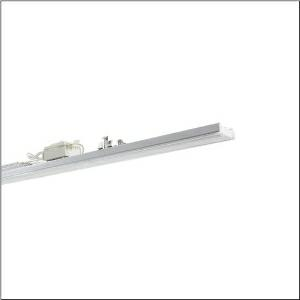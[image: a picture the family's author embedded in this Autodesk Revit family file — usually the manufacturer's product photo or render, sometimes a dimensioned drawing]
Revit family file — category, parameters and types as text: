
# Revit family: licross_11_recessed_ho_51tl11dn4exs
name_source: partatom
category: Lighting Fixtures
units: mm (PartAtom-declared; Revit-internal decimal feet)

## family parameters
Cut with Voids When Loaded = No
Host = Face
Light Source = No
Part Type = Normal
Room Calculation Point = No
Round Connector Dimension = Use Diameter
Shared = No

## types (1)
- --- (1 x LED, 14000 lm, 76.8 W, 4000K)
    Apparent Load = 77 VA
    CIE Flux Codes = 87 95 99 100 100
    Color Rendering = 80
    Color Temperature = 4000K
    Default Elevation = 1800 mm
    Description = Licross 11 Recessed HO, luminaire insert, of sheet steel, coil coated, white, length: 1.500mm, width: 66mm, height: 67mm, LED rated luminous flux: 14.000lm, light colour: 840, SDCM (Standard Deviation of Colour Matching)MacAdam ≤ 2 SDCM (initial), control gear: DALI 2, with plug, 5-pole, with phase selection, mains connection: 220..240V, AC, 50/60Hz, rated input power: 77W, internal wiring halogen-free, primary light control with lens, of plastic, primary optical cover: cover, of PMMA, light emission: direct distribution, primary light characteristic: symmetric, protection rating (complete): IP40, insulation class (complete): insulation class I (protective earthing), certification: CE, ENEC, VDE, UKCA, protection symbol: D if used in an environment without relevant dust loads with corresponding accessories, impact resistance: IK06, permissible ambient temperature for indoor applications: -25..+30°C, corresponds to IFS (International Featured Standards) requirements for safety and quality in the food industry, reducing of maximum allowable ambient temperature of 5°C with ceiling mounting, LABS conformity tested according to VDMA 24364:2018-05, The light source and the operating device comply with the requirements of the Ecodesign Regulation (EU) 2019/2020 and are replaceable in accordance with this regulation, packaging unit: 1 piece
    Height = 58 mm
    Lamp = 1 x LED
    Lamp Light Flux = 14000 lm
    Lamp Power = 76.8 W
    Lamp count = 1
    Length = 1500 mm
    Luminous efficacy = 182 lm/W
    Manufacturer = Siteco
    ModVariant = No
    Model = 51TL11DN4EXS
    Mounting Place = Ceiling
    Mounting Type = Pendant
    Number of Poles = 1
    OnlyDefault = Yes
    Power Factor = 1
    Product Name = Licross 11 Recessed HO
    Product group = luminaire insert | ceiling pendant
    ProductGroupID = 901
    Protection Class = Protection class I
    Protection Degree = IP 40
    RLX_Detail_Level = 1
    RLX_Emergency_Light_Flux = 0 lm
    RLX_Emergency_Type = 0
    RLX_Emergency_Type_DB = No
    RlxData = <blob elided: 24829 chars, md5=88943ad8>
    Socket = socket
    Standby Power = 0 W
    System Light Flux = 14000 lm
    System Power = 77 W
    Type Comments = factory setting: luminous flux: 100 % | dim-lin: 254 | 522 mA
    Type Image = l_1296930.jpg
    URL = http://relux.com
    VarID = @adj_100487
    Voltage = 0 V
    Weight = 0.00 kg
    Width = 66 mm

## geometry (parser evidence)
native form markers: Blend x4, Sweep x13
no freeform markers — native parametric forms only
